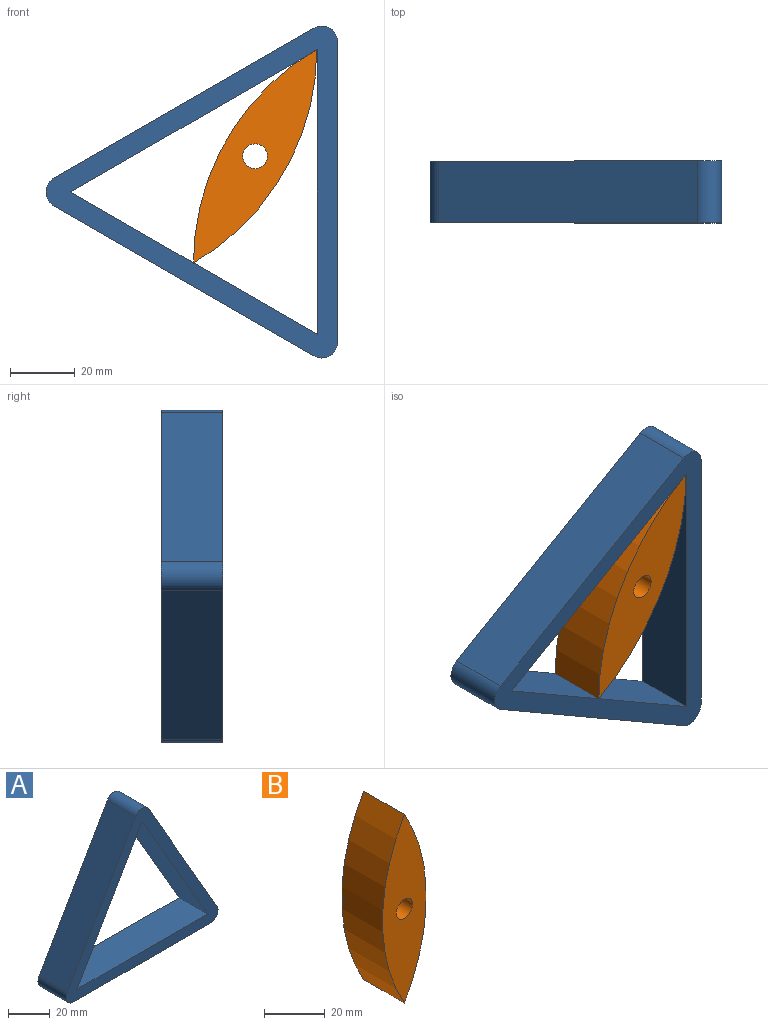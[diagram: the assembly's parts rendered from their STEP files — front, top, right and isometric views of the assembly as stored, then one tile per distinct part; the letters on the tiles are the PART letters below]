
ASSEMBLY  parts=2 mates=1
PART A: 11 faces, bbox 102.5x19.1x90.2 mm
  f0: plane 80.01x46.19mm, normal (-0.87,0,0.5), area 1760mm2, adj f6,f7,f8,f10
  f1: plane 92.39x19.05mm, normal (0,0,-1), area 1760mm2, adj f6,f7,f8,f9
  f2: plane 76.2x43.99mm, normal (-0.87,0,-0.5), area 1676.2mm2, adj f3,f4,f6,f7
  f3: plane 87.99x19.05mm, normal (0,0,1), area 1676.2mm2, adj f2,f4,f6,f7
  f4: plane 76.2x43.99mm, normal (0.87,0,-0.5), area 1676.2mm2, adj f2,f3,f6,f7
  f5: plane 80.01x46.19mm, normal (0.87,0,0.5), area 1760mm2, adj f6,f7,f9,f10
  f6: plane 102.55x90.17mm, normal (0,-1,0), area 1832.7mm2, adj f0,f1,f2,f3,f4,f5,f8,f9
  f7: plane 102.55x90.17mm, normal (0,1,0), area 1832.7mm2, adj f0,f1,f2,f3,f4,f5,f8,f9
  f8: cylinder r=5.08mm len=19.05mm, axis (0,1,0), area 202.7mm2, adj f0,f1,f6,f7
  f9: cylinder r=5.08mm len=19.05mm, axis (0,1,0), area 202.7mm2, adj f1,f5,f6,f7
  f10: cylinder r=5.08mm len=19.05mm, axis (0,1,0), area 202.7mm2, adj f0,f5,f6,f7
PART B: 5 faces, bbox 20.4x19.1x76.2 mm
  f0: cylinder r=76.2mm len=76.2mm, axis (0,1,0), area 1520.1mm2, adj f1,f2,f3
  f1: cylinder r=76.2mm len=76.2mm, axis (0,1,0), area 1520.1mm2, adj f0,f2,f3
  f2: plane 76.2x20.42mm, normal (0,-1,0), area 1006.4mm2, adj f0,f1,f4
  f3: plane 76.2x20.42mm, normal (0,1,0), area 1006.4mm2, adj f0,f1,f4
  f4: cylinder r=3.81mm len=19.05mm, axis (0,-1,0), area 456mm2, adj f2,f3
PLACE A rot(axis=(0,1,0),30deg) t=(-9.57,9.52,21.31)mm
PLACE B rot(axis=(0,1,0),30deg) t=(-9.75,9.52,21.35)mm
MATE parallel A.f7 <-> B.f4  axis (0,1,0) through (-9.57,9.52,21.31)mm
